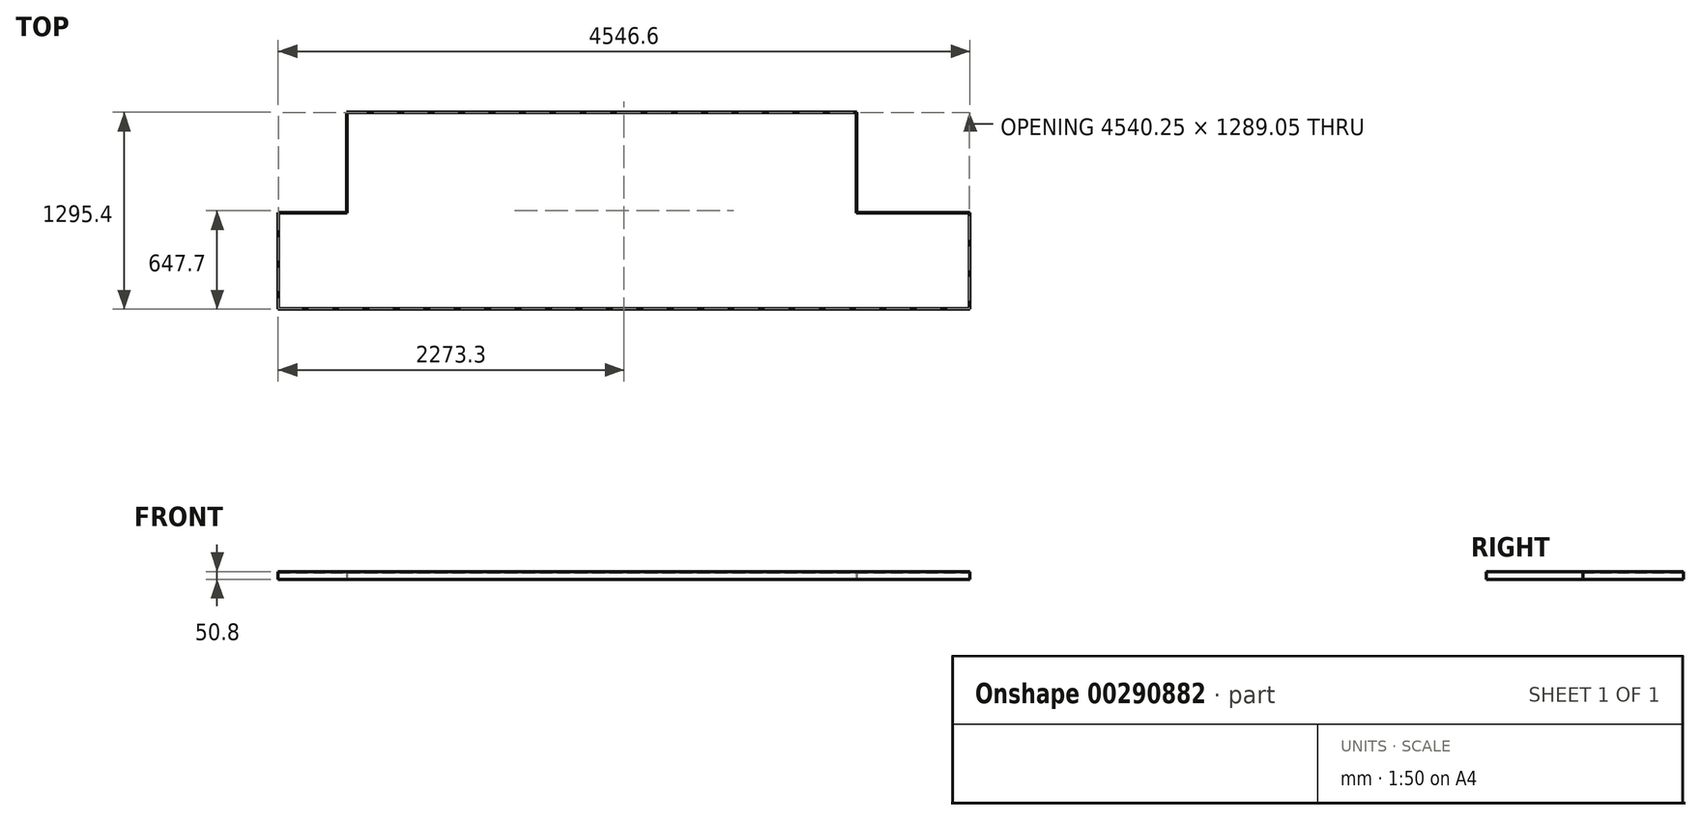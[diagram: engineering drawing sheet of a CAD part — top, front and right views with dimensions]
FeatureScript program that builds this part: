
annotation { "Feature Type Name" : "Feature", "Feature Type Description" : "" }
export const myFeature = defineFeature(function(context is Context, id is Id, definition is map)
    precondition{}
    {
        {
            var Q0;
            Q0=qCreatedBy(makeId("Top.planeOp"),FACE);
            var sketch = newSketch(context, id + "F0", { "sketchPlane" : qUnion([Q0])});
            skLineSegment(sketch, "E0.bottom", {"start": v(0, 0) * mm, "end": v(450.32, 0) * mm});
            skLineSegment(sketch, "E0.top", {"start": v(0, -635) * mm, "end": v(4546.6, -635) * mm});
            skLineSegment(sketch, "E0.left", {"start": v(0, 0) * mm, "end": v(0, -635) * mm});
            skLineSegment(sketch, "E0.right", {"start": v(4546.6, 0) * mm, "end": v(4546.6, -635) * mm});
            skLineSegment(sketch, "E1.top", {"start": v(450.32, 660.4) * mm, "end": v(3803.12, 660.4) * mm});
            skLineSegment(sketch, "E1.left", {"start": v(450.32, 0) * mm, "end": v(450.32, 660.4) * mm});
            skLineSegment(sketch, "E1.right", {"start": v(3803.12, 0) * mm, "end": v(3803.12, 660.4) * mm});
            skLineSegment(sketch, "E2.trimOffspring", {"start": v(3803.12, 0) * mm, "end": v(4546.6, 0) * mm});
            skLineSegment(sketch, "E3.0", {"start": v(453.5, -3.18) * mm, "end": v(453.5, 657.22) * mm});
            skLineSegment(sketch, "E3.1", {"start": v(3.18, -3.18) * mm, "end": v(453.5, -3.18) * mm});
            skLineSegment(sketch, "E3.2", {"start": v(453.5, 657.22) * mm, "end": v(3799.95, 657.22) * mm});
            skLineSegment(sketch, "E3.3", {"start": v(3.18, -3.18) * mm, "end": v(3.18, -631.83) * mm});
            skLineSegment(sketch, "E3.4", {"start": v(3799.95, -3.18) * mm, "end": v(3799.95, 657.22) * mm});
            skLineSegment(sketch, "E3.5", {"start": v(3799.95, -3.18) * mm, "end": v(4543.43, -3.18) * mm});
            skLineSegment(sketch, "E3.6", {"start": v(4543.43, -3.18) * mm, "end": v(4543.43, -631.83) * mm});
            skLineSegment(sketch, "E3.7", {"start": v(3.18, -631.83) * mm, "end": v(4543.43, -631.83) * mm});
            skSolve(sketch);
        }
        {
            var Q0;
            Q0 = qSketchRegion(id + "F0", true);
            extrude(context, id + "F1", {"entities" : qUnion([Q0]), "depth" : 50.8 * mm});
        }
        {
            var Q0;
            Q0=makeQuery(id+"F0.imprint","IMPRINT",FACE,{"disambiguationData":[TD([[makeQuery(id+"F0.imprint","IMPRINT",EDGE,{"derivedFrom":sQuery(id+"F0.wireOp",EDGE,"E3.0")}),-1.0]])]});
            extrude(context, id + "F2", {"entities" : qUnion([Q0]), "depth" : 44.45 * mm});
        }
        {
            var Q0;
            Q0=makeQuery(id+"F2.opExtrude","CAP_FACE",FACE,{"disambiguationData":[OSD([sQuery(id+"F0.wireOp",EDGE,"E3.0"),sQuery(id+"F0.wireOp",EDGE,"E3.1"),sQuery(id+"F0.wireOp",EDGE,"E3.2"),sQuery(id+"F0.wireOp",EDGE,"E3.3"),sQuery(id+"F0.wireOp",EDGE,"E3.4"),sQuery(id+"F0.wireOp",EDGE,"E3.5"),sQuery(id+"F0.wireOp",EDGE,"E3.6"),sQuery(id+"F0.wireOp",EDGE,"E3.7")])],"isStart":false});
            var sketch = newSketch(context, id + "F3", { "sketchPlane" : qUnion([Q0])});
            skLineSegment(sketch, "E4", {"start": v(453.5, 657.22) * mm, "end": v(453.5, -3.18) * mm});
            skLineSegment(sketch, "E5", {"start": v(453.5, -3.18) * mm, "end": v(3.18, -3.18) * mm});
            skLineSegment(sketch, "E6", {"start": v(3.18, -3.18) * mm, "end": v(3.18, -631.83) * mm});
            skLineSegment(sketch, "E7", {"start": v(3.18, -631.83) * mm, "end": v(4543.43, -631.83) * mm});
            skLineSegment(sketch, "E8", {"start": v(4543.43, -631.83) * mm, "end": v(4543.43, -3.18) * mm});
            skLineSegment(sketch, "E9", {"start": v(4543.43, -3.18) * mm, "end": v(3799.95, -3.18) * mm});
            skLineSegment(sketch, "E10", {"start": v(3799.95, -3.18) * mm, "end": v(3799.95, 657.22) * mm});
            skLineSegment(sketch, "E11", {"start": v(3799.95, 657.22) * mm, "end": v(453.5, 657.22) * mm});
            skSolve(sketch);
        }
        {
            var Q0;
            Q0 = qSketchRegion(id + "F3", true);
            extrude(context, id + "F4", {"entities" : qUnion([Q0]), "depth" : 6.35 * mm});
        }
    });
